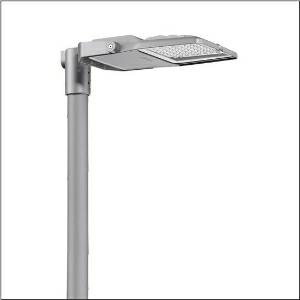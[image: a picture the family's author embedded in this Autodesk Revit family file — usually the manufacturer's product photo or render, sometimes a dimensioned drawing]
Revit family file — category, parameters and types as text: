
# Revit family: floodlight_fl_21_mini___pl61_5xa7772c2c3a_5552
name_source: partatom
category: Lighting Fixtures
units: mm (PartAtom-declared; Revit-internal decimal feet)

## family parameters
Cut with Voids When Loaded = No
Host = Face
Light Source = No
Part Type = Normal
Room Calculation Point = No
Round Connector Dimension = Use Diameter
Shared = No

## types (1)
- --- (1 x LED, 11980 lm, 87.2 W, 3000K)
    Apparent Load = 87 VA
    CIE Flux Codes = 33 65 98 100 100
    Color Rendering = 70
    Color Temperature = 3000K
    Default Elevation = 1800 mm
    Description = Floodlight FL 21 mini, floodlight, primary light control with lens, of PMMA, primary optical cover: protective disc, of toughened safety glass, transparent, light distribution: PL61, light emission: direct distribution, installation type: surface-mounted, LED, High Power LED, rated luminous flux: 11.980lm, luminous efficacy: 137lm/W, light colour: 730, colour temperature: 3000K, control gear: ECG iQ, control: Auto-Match, Temp-Guard, Night-Set, Smart-Wire, Desk-Remote (wireless, voltage-free reading and setting of iQ features in the workshop via application-optimized NFC function/RFID function), optimised constant luminous flux control (CLO 2.0), Light-Fading, Lumen-Switch, with terminal, 6-pole, mains connection: 220..240V, AC, 50/60Hz, start of lifetime: 87W, end of lifetime: 92W, reduction: 40W, luminaire housing, of diecast aluminium, powder-coated, Siteco® metallic grey (DB 702S), corrosivity category C5 according to DIN EN ISO 12944, mast bracket, of steel, galvanised, powder-coated, protection rating (complete): IP66, insulation class (complete): insulation class II (safety insulation), certification: CE, ENEC, VDE, protection symbol: D, impact resistance: IK08, permissible operating ambient temperature: -40..+40°C, permissible operating ambient temperature for outdoor applications: -40..+50°C, standard: DIN EN 12944, packaging unit: 1 piece

Light Distribution: PL61
    Height = 70 mm
    Lamp = 1 x LED
    Lamp Light Flux = 11980 lm
    Lamp Power = 87.2 W
    Lamp count = 1
    Length = 485 mm
    Luminous efficacy = 137 lm/W
    Manufacturer = Siteco
    ModVariant = No
    Model = 5XA7772C2C3A
    Number of Poles = 1
    OnlyDefault = Yes
    Power Factor = 1
    Product Name = Floodlight FL 21 mini | PL61
    Product group = floodlight | pylon top
    ProductGroupID = 6101
    Protection Class = Protection class II
    Protection Degree = IP 66
    RLX_Detail_Level = 1
    RlxData = <blob elided: 101289 chars, md5=61215fd4>
    Socket = socket
    Standby Power = 0 W
    System Light Flux = 11980 lm
    System Power = 87 W
    Type Comments = factory setting: luminous flux: 100 % | dim-lin: 254 | 456 mA
    Type Image = l_1007125.jpg
    URL = http://relux.com
    VarID = @adj_085369
    Voltage = 0 V
    Weight = 0.00 kg
    Width = 337 mm

## geometry (parser evidence)
native form markers: Blend x4, Sweep x12
no freeform markers — native parametric forms only
